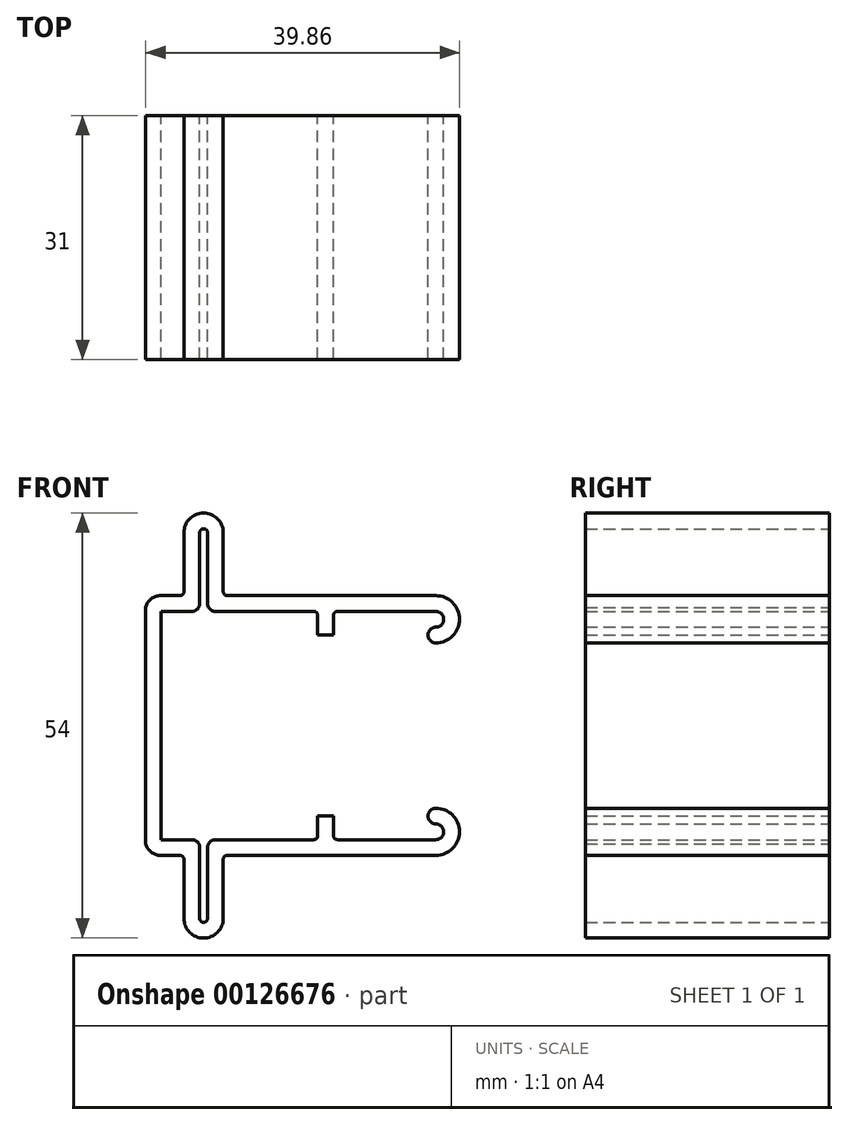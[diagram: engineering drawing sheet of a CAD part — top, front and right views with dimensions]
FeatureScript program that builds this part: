
annotation { "Feature Type Name" : "Feature", "Feature Type Description" : "" }
export const myFeature = defineFeature(function(context is Context, id is Id, definition is map)
    precondition{}
    {
        {
            var Q0;
            Q0=qCreatedBy(makeId("Front.planeOp"),FACE);
            var sketch = newSketch(context, id + "F0", { "sketchPlane" : qUnion([Q0])});
            skLineSegment(sketch, "E0.0", {"start": v(-26.54, 27.32) * mm, "end": v(-14.04, 27.32) * mm});
            skArc(sketch, "E1", {"start": v(-14.04, 27.32) * mm, "mid": v(-13.04, 26.32) * mm, "end": v(-14.04, 25.32) * mm});
            skArc(sketch, "E2.0", {"start": v(-14.04, 29.32) * mm, "mid": v(-11.04, 26.32) * mm, "end": v(-14.04, 23.32) * mm});
            skArc(sketch, "E3", {"start": v(-14.04, 25.32) * mm, "mid": v(-15.04, 24.32) * mm, "end": v(-14.04, 23.32) * mm});
            skLineSegment(sketch, "E4", {"start": v(-27.04, 26.82) * mm, "end": v(-27.04, 24.32) * mm});
            skLineSegment(sketch, "E5", {"start": v(-27.04, 24.32) * mm, "end": v(-29.04, 24.32) * mm});
            skLineSegment(sketch, "E6", {"start": v(-29.04, 24.32) * mm, "end": v(-29.04, 26.82) * mm});
            skLineSegment(sketch, "E7", {"start": v(-29.54, 27.32) * mm, "end": v(-42.04, 27.32) * mm});
            skLineSegment(sketch, "E8", {"start": v(-43.04, 28.32) * mm, "end": v(-43.04, 37.32) * mm});
            skLineSegment(sketch, "E9", {"start": v(-44.04, 37.32) * mm, "end": v(-44.04, 28.32) * mm});
            skLineSegment(sketch, "E10", {"start": v(-45.04, 27.32) * mm, "end": v(-48.97, 27.32) * mm});
            skPoint(sketch, "E11.visualSharp", {"position": v(-43.04, 27.32) * mm});
            skArc(sketch, "E11.filletArc", {"start": v(-43.04, 28.32) * mm, "mid": v(-42.75, 27.61) * mm, "end": v(-42.04, 27.32) * mm});
            skPoint(sketch, "E12.visualSharp", {"position": v(-44.04, 27.32) * mm});
            skArc(sketch, "E12.filletArc", {"start": v(-45.04, 27.32) * mm, "mid": v(-44.34, 27.61) * mm, "end": v(-44.04, 28.32) * mm});
            skArc(sketch, "E13", {"start": v(-43.04, 37.32) * mm, "mid": v(-43.54, 37.82) * mm, "end": v(-44.04, 37.32) * mm});
            skArc(sketch, "E14.0", {"start": v(-41.04, 37.32) * mm, "mid": v(-43.54, 39.82) * mm, "end": v(-46.04, 37.32) * mm});
            skLineSegment(sketch, "E15.0", {"start": v(-41.04, 29.82) * mm, "end": v(-41.04, 37.32) * mm});
            skLineSegment(sketch, "E16.0", {"start": v(-46.04, 37.32) * mm, "end": v(-46.04, 29.82) * mm});
            skLineSegment(sketch, "E17", {"start": v(-40.54, 29.32) * mm, "end": v(-14.04, 29.32) * mm});
            skLineSegment(sketch, "E18", {"start": v(-46.54, 29.32) * mm, "end": v(-48.97, 29.32) * mm});
            skLineSegment(sketch, "E19", {"start": v(-46.04, 37.32) * mm, "end": v(-39.75, 37.32) * mm, "construction": true});
            skArc(sketch, "E20", {"start": v(-48.97, 29.32) * mm, "mid": v(-50.19, 28.9) * mm, "end": v(-50.9, 27.83) * mm});
            skLineSegment(sketch, "E21", {"start": v(-48.97, 27.32) * mm, "end": v(-48.97, 12.82) * mm});
            skLineSegment(sketch, "E22", {"start": v(-50.9, 27.83) * mm, "end": v(-50.9, 12.82) * mm});
            skLineSegment(sketch, "E23", {"start": v(-64.33, 12.82) * mm, "end": v(-4.22, 12.82) * mm, "construction": true});
            skPoint(sketch, "E24.visualSharp", {"position": v(-41.04, 29.32) * mm});
            skArc(sketch, "E24.filletArc", {"start": v(-41.04, 29.82) * mm, "mid": v(-40.9, 29.46) * mm, "end": v(-40.54, 29.32) * mm});
            skPoint(sketch, "E25.visualSharp", {"position": v(-46.04, 29.32) * mm});
            skArc(sketch, "E25.filletArc", {"start": v(-46.54, 29.32) * mm, "mid": v(-46.19, 29.46) * mm, "end": v(-46.04, 29.82) * mm});
            skPoint(sketch, "E26.visualSharp", {"position": v(-29.04, 27.32) * mm});
            skArc(sketch, "E26.filletArc", {"start": v(-29.04, 26.82) * mm, "mid": v(-29.19, 27.17) * mm, "end": v(-29.54, 27.32) * mm});
            skPoint(sketch, "E27.visualSharp", {"position": v(-27.04, 27.32) * mm});
            skArc(sketch, "E27.filletArc", {"start": v(-26.54, 27.32) * mm, "mid": v(-26.9, 27.17) * mm, "end": v(-27.04, 26.82) * mm});
            skArc(sketch, "E28.MirrorCS", {"start": v(-41.04, -4.18) * mm, "mid": v(-40.9, -3.83) * mm, "end": v(-40.54, -3.68) * mm});
            skArc(sketch, "E29.MirrorCS", {"start": v(-46.54, -3.68) * mm, "mid": v(-46.19, -3.83) * mm, "end": v(-46.04, -4.18) * mm});
            skArc(sketch, "E30.MirrorCS", {"start": v(-26.54, -1.68) * mm, "mid": v(-26.9, -1.54) * mm, "end": v(-27.04, -1.18) * mm});
            skArc(sketch, "E31.MirrorCS", {"start": v(-29.04, -1.18) * mm, "mid": v(-29.19, -1.54) * mm, "end": v(-29.54, -1.68) * mm});
            skArc(sketch, "E32.MirrorCS", {"start": v(-45.04, -1.68) * mm, "mid": v(-44.34, -1.97) * mm, "end": v(-44.04, -2.68) * mm});
            skArc(sketch, "E33.MirrorCS", {"start": v(-43.04, -2.68) * mm, "mid": v(-42.75, -1.97) * mm, "end": v(-42.04, -1.68) * mm});
            skArc(sketch, "E34.MirrorCS", {"start": v(-43.04, -11.68) * mm, "mid": v(-43.54, -12.18) * mm, "end": v(-44.04, -11.68) * mm});
            skLineSegment(sketch, "E35.MirrorCS", {"start": v(-46.04, -11.68) * mm, "end": v(-46.04, -4.18) * mm});
            skLineSegment(sketch, "E36.MirrorCS", {"start": v(-46.54, -3.68) * mm, "end": v(-48.97, -3.68) * mm});
            skPoint(sketch, "E37.MirrorP", {"position": v(-43.04, -1.68) * mm});
            skArc(sketch, "E38.MirrorCS", {"start": v(-48.97, -3.68) * mm, "mid": v(-50.19, -3.27) * mm, "end": v(-50.9, -2.2) * mm});
            skLineSegment(sketch, "E39.MirrorCS", {"start": v(-50.9, -2.2) * mm, "end": v(-50.9, 12.82) * mm});
            skPoint(sketch, "E40.MirrorP", {"position": v(-29.04, -1.68) * mm});
            skLineSegment(sketch, "E41.MirrorCS", {"start": v(-29.54, -1.68) * mm, "end": v(-42.04, -1.68) * mm});
            skPoint(sketch, "E42.MirrorP", {"position": v(-41.04, -3.68) * mm});
            skPoint(sketch, "E43.MirrorP", {"position": v(-27.04, -1.68) * mm});
            skArc(sketch, "E44.MirrorCS", {"start": v(-41.04, -11.68) * mm, "mid": v(-43.54, -14.18) * mm, "end": v(-46.04, -11.68) * mm});
            skLineSegment(sketch, "E45.MirrorCS", {"start": v(-46.04, -11.68) * mm, "end": v(-39.75, -11.68) * mm, "construction": true});
            skArc(sketch, "E46.MirrorCS", {"start": v(-14.04, -1.68) * mm, "mid": v(-13.04, -0.68) * mm, "end": v(-14.04, 0.32) * mm});
            skLineSegment(sketch, "E47.MirrorCS", {"start": v(-27.04, 1.32) * mm, "end": v(-29.04, 1.32) * mm});
            skLineSegment(sketch, "E48.MirrorCS", {"start": v(-27.04, -1.18) * mm, "end": v(-27.04, 1.32) * mm});
            skLineSegment(sketch, "E49.MirrorCS", {"start": v(-45.04, -1.68) * mm, "end": v(-48.97, -1.68) * mm});
            skLineSegment(sketch, "E50.MirrorCS", {"start": v(-29.04, 1.32) * mm, "end": v(-29.04, -1.18) * mm});
            skLineSegment(sketch, "E51.MirrorCS", {"start": v(-40.54, -3.68) * mm, "end": v(-14.04, -3.68) * mm});
            skPoint(sketch, "E52.MirrorP", {"position": v(-46.04, -3.68) * mm});
            skPoint(sketch, "E53.MirrorP", {"position": v(-44.04, -1.68) * mm});
            skLineSegment(sketch, "E54.MirrorCS", {"start": v(-41.04, -4.18) * mm, "end": v(-41.04, -11.68) * mm});
            skLineSegment(sketch, "E55.MirrorCS", {"start": v(-26.54, -1.68) * mm, "end": v(-14.04, -1.68) * mm});
            skLineSegment(sketch, "E56.MirrorCS", {"start": v(-48.97, -1.68) * mm, "end": v(-48.97, 12.82) * mm});
            skArc(sketch, "E57.MirrorCS", {"start": v(-14.04, -3.68) * mm, "mid": v(-11.04, -0.68) * mm, "end": v(-14.04, 2.32) * mm});
            skLineSegment(sketch, "E58.MirrorCS", {"start": v(-44.04, -11.68) * mm, "end": v(-44.04, -2.68) * mm});
            skLineSegment(sketch, "E59.MirrorCS", {"start": v(-43.04, -2.68) * mm, "end": v(-43.04, -11.68) * mm});
            skArc(sketch, "E60.MirrorCS", {"start": v(-14.04, 0.32) * mm, "mid": v(-15.04, 1.32) * mm, "end": v(-14.04, 2.32) * mm});
            skSolve(sketch);
        }
        {
            var Q0;
            Q0 = qSketchRegion(id + "F0", true);
            extrude(context, id + "F1", {"entities" : qUnion([Q0]), "depth" : 31 * mm});
        }
    });
